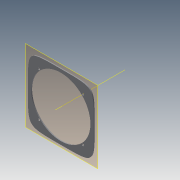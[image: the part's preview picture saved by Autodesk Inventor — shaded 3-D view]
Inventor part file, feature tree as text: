
AUTODESK INVENTOR PART (.ipt)
format: ipt  version: 2014 SP1 (Build 180222100, 222)  size: 117,248 bytes
history: native  units: in
note: dims shown in document units (in); Inventor stores cm internally (conversion verified against a paired STEP export)
features: reference x8, plane x1, extrude x1, other x1, sketch x1
ambient origin geometry x8: Origin, YZ Plane, XZ Plane, XY Plane, X Axis, Y Axis, Z Axis, Center Point
bodies: Solid1 (feature_tree)
feature tree (12):
  plane  "Work Plane1"
  extrude  "Extrusion1"  Depth=5.0in
  other  "Work Axis1"
  sketch  "Sketch1"  dims[d0=5.0in d1=5.0in d2=2.5in d3=2.5in d4=6.75in d5=0.1083in d6=0.0in d7=0.25in d8=0.25in d9=0.25in d10=0.25in]
  reference  "Reference1"
  reference  "Reference2"
  reference  "Reference3"
  reference  "Reference4"
  reference  "Reference5"
  reference  "Reference6"
  reference  "Reference7"
  reference  "Reference8"
